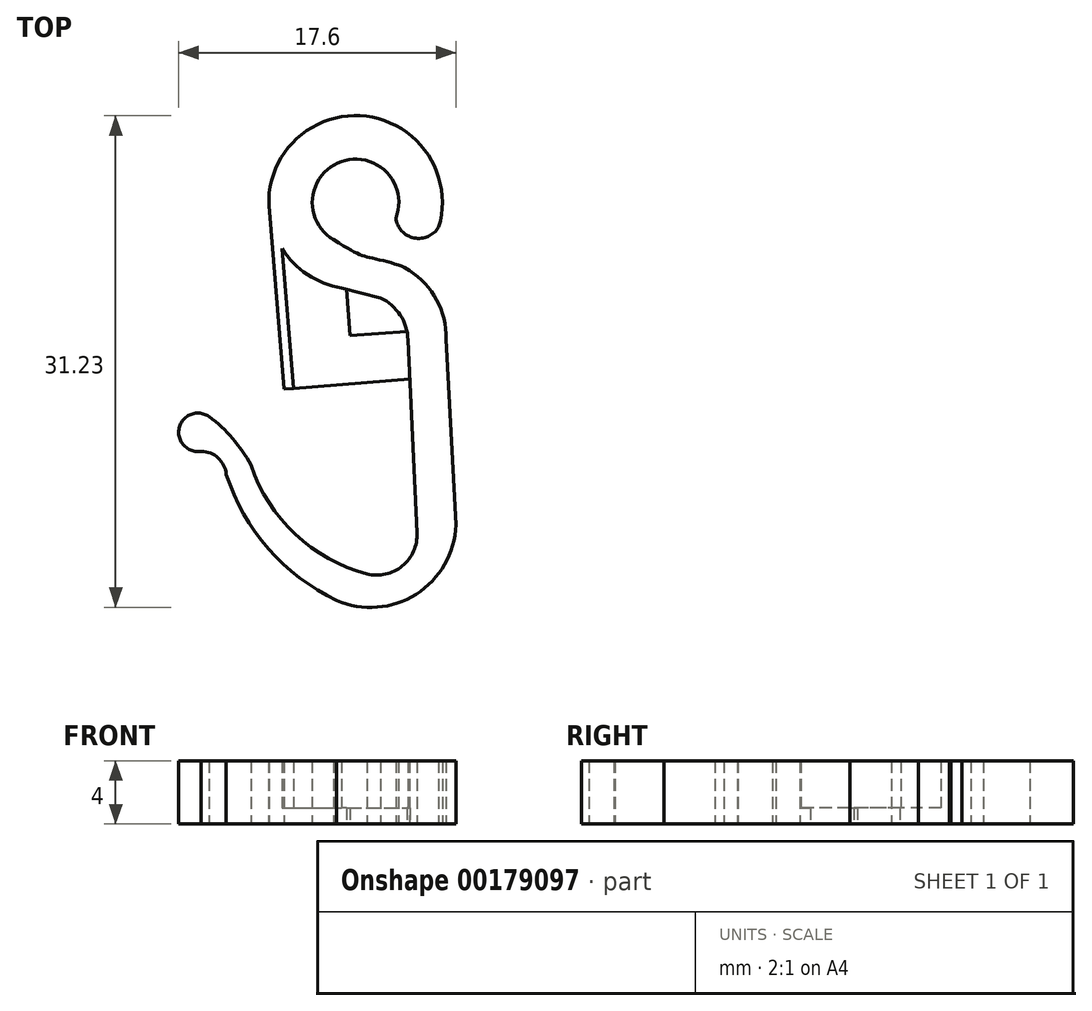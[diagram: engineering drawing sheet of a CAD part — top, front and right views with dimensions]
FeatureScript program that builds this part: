
annotation { "Feature Type Name" : "Feature", "Feature Type Description" : "" }
export const myFeature = defineFeature(function(context is Context, id is Id, definition is map)
    precondition{}
    {
        {
            var Q0;
            Q0=qCreatedBy(makeId("Top.planeOp"),FACE);
            var sketch = newSketch(context, id + "F0", { "sketchPlane" : qUnion([Q0])});
            skPoint(sketch, "E0.middle", {"position": v(0, 0) * mm});
            skArc(sketch, "E1", {"start": v(2.56, 9.22) * mm, "mid": v(-0.9, 12.8) * mm, "end": v(-1.4, 7.84) * mm});
            skArc(sketch, "E2", {"start": v(5.28, 8.65) * mm, "mid": v(-2.93, 14.88) * mm, "end": v(-0.9, 4.78) * mm});
            skArc(sketch, "E3", {"start": v(2.56, 9.22) * mm, "mid": v(3.72, 7.96) * mm, "end": v(5.28, 8.65) * mm});
            skPoint(sketch, "E3.first.point", {"position": v(2.56, 9.22) * mm});
            skPoint(sketch, "E3.second.point", {"position": v(5.28, 8.65) * mm});
            skPoint(sketch, "E3.third.point", {"position": v(3.46, 8.03) * mm});
            skArc(sketch, "E4", {"start": v(3.33, 1.48) * mm, "mid": v(2.84, 3.06) * mm, "end": v(1.6, 4.15) * mm});
            skPoint(sketch, "E4.first.point", {"position": v(1.6, 4.15) * mm});
            skPoint(sketch, "E4.second.point", {"position": v(3.05, 2.67) * mm});
            skPoint(sketch, "E4.third.point", {"position": v(3.33, 1.48) * mm});
            skLineSegment(sketch, "E5", {"start": v(1.6, 4.15) * mm, "end": v(-0.9, 4.78) * mm});
            skArc(sketch, "E6", {"start": v(5.75, 1.53) * mm, "mid": v(5.16, 4.02) * mm, "end": v(3.41, 5.89) * mm});
            skPoint(sketch, "E6.first.point", {"position": v(3.41, 5.89) * mm});
            skPoint(sketch, "E6.second.point", {"position": v(4.98, 4.33) * mm});
            skPoint(sketch, "E6.third.point", {"position": v(5.75, 1.8) * mm});
            skLineSegment(sketch, "E7", {"start": v(3.33, 1.48) * mm, "end": v(3.9, -10.78) * mm});
            skLineSegment(sketch, "E8", {"start": v(5.75, 1.53) * mm, "end": v(6.37, -10.28) * mm});
            skArc(sketch, "E9", {"start": v(0.72, -13.4) * mm, "mid": v(2.97, -12.88) * mm, "end": v(3.9, -10.78) * mm});
            skPoint(sketch, "E9.second.point", {"position": v(3.12, -12.75) * mm});
            skPoint(sketch, "E9.third.point", {"position": v(2.03, -13.37) * mm});
            skArc(sketch, "E10", {"start": v(-1.74, -14.8) * mm, "mid": v(3.6, -14.83) * mm, "end": v(6.37, -10.28) * mm});
            skPoint(sketch, "E10.second.point", {"position": v(5.27, -13.37) * mm});
            skPoint(sketch, "E10.third.point", {"position": v(4.52, -14.18) * mm});
            skArc(sketch, "E11", {"start": v(-8.21, -7.06) * mm, "mid": v(-5.53, -11.79) * mm, "end": v(-1.2, -15.06) * mm});
            skPoint(sketch, "E11.first.point", {"position": v(-1.74, -14.8) * mm});
            skPoint(sketch, "E11.second.point", {"position": v(-4.57, -12.78) * mm});
            skPoint(sketch, "E11.third.point", {"position": v(-8.21, -7.06) * mm});
            skArc(sketch, "E12", {"start": v(-6.65, -6.48) * mm, "mid": v(-3.83, -10.86) * mm, "end": v(0.72, -13.4) * mm});
            skPoint(sketch, "E12.first.point", {"position": v(0.72, -13.4) * mm});
            skPoint(sketch, "E12.second.point", {"position": v(-2.38, -12) * mm});
            skPoint(sketch, "E12.third.point", {"position": v(-6.65, -6.48) * mm});
            skFitSpline(sketch, "E13", {"points": [v(-1.55, 7.94) * mm, v(1.03, 6.68) * mm, v(3.41, 5.89) * mm], "startDerivative": vector(9, -5.72) * mm, "endDerivative": vector(2.71, -2.26) * mm});
            skArc(sketch, "E14", {"start": v(-9.25, -3.44) * mm, "mid": v(-11.2, -4.09) * mm, "end": v(-9.8, -5.6) * mm});
            skPoint(sketch, "E14.first.point", {"position": v(-10.97, -5.15) * mm});
            skPoint(sketch, "E14.second.point", {"position": v(-10.71, -3.4) * mm});
            skPoint(sketch, "E14.third.point", {"position": v(-9.3, -3.4) * mm});
            skArc(sketch, "E15", {"start": v(-8.21, -7.06) * mm, "mid": v(-8.73, -6.02) * mm, "end": v(-9.8, -5.6) * mm});
            skPoint(sketch, "E15.second.point", {"position": v(-9.8, -5.6) * mm});
            skPoint(sketch, "E15.third.point", {"position": v(-8.95, -5.85) * mm});
            skArc(sketch, "E16", {"start": v(-6.65, -6.48) * mm, "mid": v(-7.8, -4.79) * mm, "end": v(-9.3, -3.4) * mm});
            skPoint(sketch, "E16.second.point", {"position": v(-7.83, -4.76) * mm});
            skLineSegment(sketch, "E17", {"start": v(-5.5, 10) * mm, "end": v(-4.55, -1.65) * mm});
            skLineSegment(sketch, "E18", {"start": v(-4.55, -1.65) * mm, "end": v(3.45, -1) * mm});
            skLineSegment(sketch, "E19", {"start": v(-0.58, 4.7) * mm, "end": v(-0.36, 1.77) * mm});
            skLineSegment(sketch, "E20", {"start": v(-0.36, 1.77) * mm, "end": v(3.27, 2) * mm});
            skLineSegment(sketch, "E21", {"start": v(-4.67, 7.29) * mm, "end": v(-3.94, -1.6) * mm});
            skSolve(sketch);
        }
        {
            var Q0;
            {var subQ8=sQuery(id+"F0.wireOp",EDGE,"E6");Q0=makeQuery(id+"F0.imprint","IMPRINT",FACE,{"disambiguationData":[TD([[makeQuery(id+"F0.imprint","IMPRINT",EDGE,{"derivedFrom":subQ8}),1.0]])]});}
            extrude(context, id + "F1", {"entities" : qUnion([Q0]), "depth" : 4 * mm});
        }
        {
            var Q0;
            {var subQ8=sQuery(id+"F0.wireOp",EDGE,"E19");Q0=makeQuery(id+"F0.imprint","IMPRINT",FACE,{"disambiguationData":[TD([[makeQuery(id+"F0.imprint","IMPRINT",EDGE,{"derivedFrom":subQ8}),-1.0]])]});}
            extrude(context, id + "F2", {"entities" : qUnion([Q0]), "operationType" : NewBodyOperationType.ADD, "depth" : 1 * mm});
        }
        {
            var Q0;
            {var subQ0=sQuery(id+"F0.wireOp",EDGE,"E21");Q0=makeQuery(id+"F0.imprint","IMPRINT",FACE,{"disambiguationData":[TD([[makeQuery(id+"F0.imprint","IMPRINT",EDGE,{"derivedFrom":subQ0}),-1.0]])]});}
            extrude(context, id + "F3", {"entities" : qUnion([Q0]), "operationType" : NewBodyOperationType.ADD, "depth" : 4 * mm});
        }
    });
